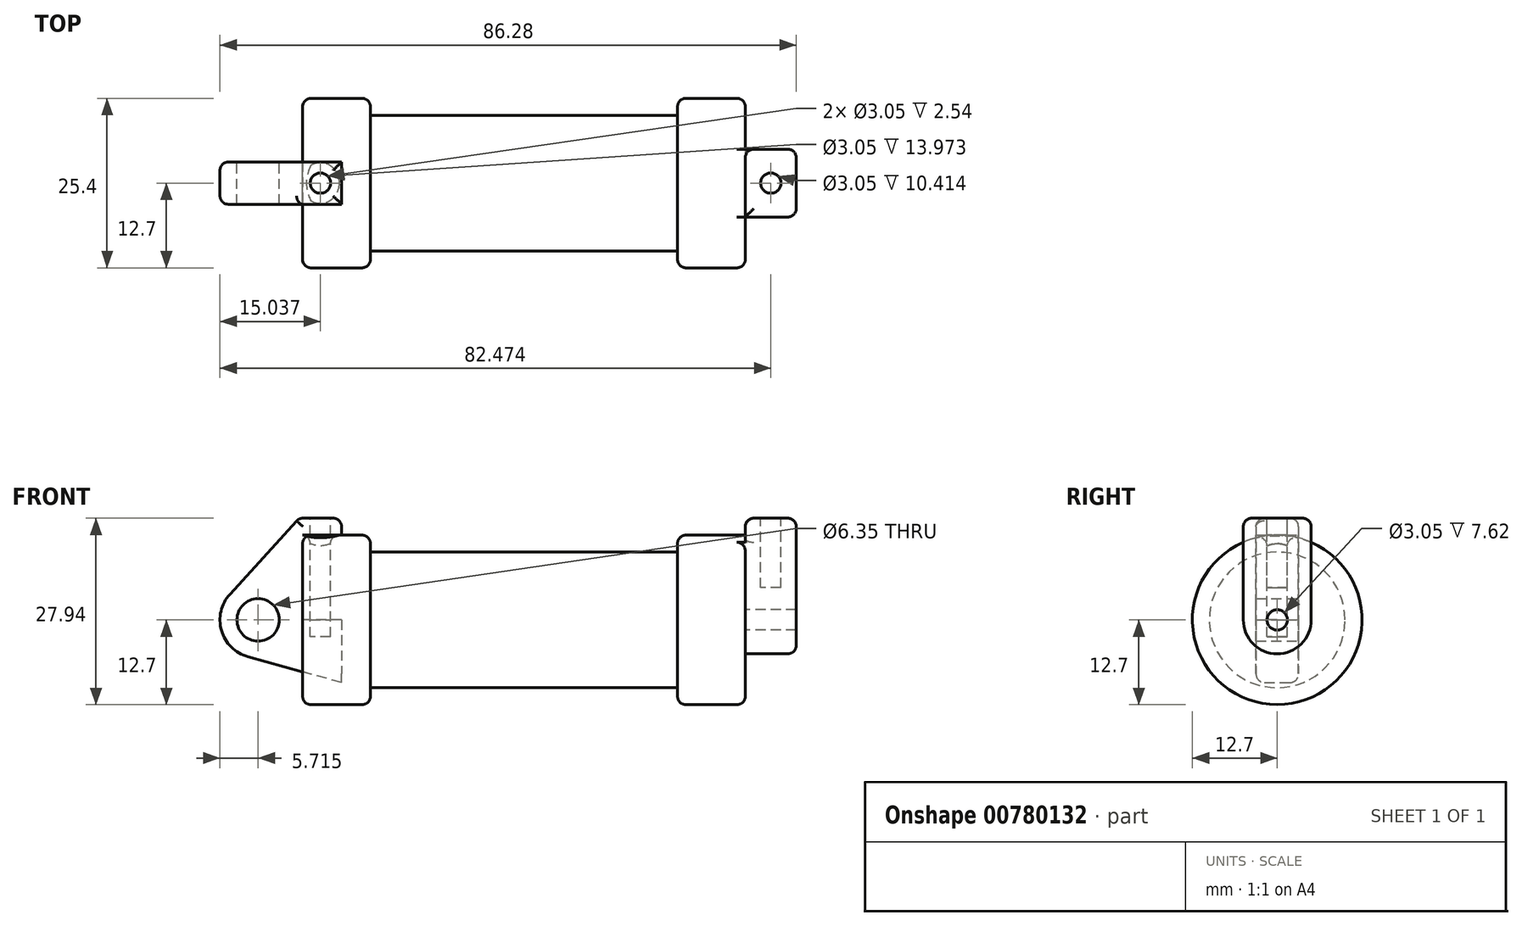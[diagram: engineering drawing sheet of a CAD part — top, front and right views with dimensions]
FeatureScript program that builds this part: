
annotation { "Feature Type Name" : "Feature", "Feature Type Description" : "" }
export const myFeature = defineFeature(function(context is Context, id is Id, definition is map)
    precondition{}
    {
        {
            var Q0;
            Q0=qCreatedBy(makeId("Front.planeOp"),FACE);
            var sketch = newSketch(context, id + "F0", { "sketchPlane" : qUnion([Q0])});
            skLineSegment(sketch, "E0", {"start": v(0, 0) * mm, "end": v(0, 12.7) * mm});
            skLineSegment(sketch, "E1", {"start": v(0, 12.7) * mm, "end": v(10.16, 12.7) * mm});
            skLineSegment(sketch, "E2", {"start": v(10.16, 12.7) * mm, "end": v(10.16, 10.16) * mm});
            skLineSegment(sketch, "E3", {"start": v(10.16, 10.16) * mm, "end": v(56.13, 10.16) * mm});
            skLineSegment(sketch, "E4", {"start": v(56.13, 10.16) * mm, "end": v(56.13, 12.7) * mm});
            skLineSegment(sketch, "E5", {"start": v(56.13, 12.7) * mm, "end": v(66.3, 12.7) * mm});
            skLineSegment(sketch, "E6", {"start": v(66.3, 12.7) * mm, "end": v(66.3, 0) * mm});
            skLineSegment(sketch, "E7", {"start": v(66.3, 0) * mm, "end": v(0, 0) * mm});
            skLineSegment(sketch, "E8", {"start": v(5.84, 15.24) * mm, "end": v(-0.5, 15.24) * mm});
            skLineSegment(sketch, "E9", {"start": v(-0.5, 15.24) * mm, "end": v(-10.88, 3.85) * mm});
            skLineSegment(sketch, "E10", {"start": v(0, 0) * mm, "end": v(-6.65, 0) * mm});
            skCircle(sketch, "E11", {"center": v(-6.65, 0) * mm, "radius": 5.72 * mm});
            skCircle(sketch, "E12", {"center": v(-6.65, 0) * mm, "radius": 3.18 * mm});
            skLineSegment(sketch, "E13", {"start": v(5.84, 15.24) * mm, "end": v(5.84, -9.4) * mm});
            skLineSegment(sketch, "E14", {"start": v(5.84, -9.4) * mm, "end": v(-8.18, -5.5) * mm});
            skSolve(sketch);
        }
        {
            var Q0;
            {var subQ0=sQuery(id+"F0.wireOp",EDGE,"E2");Q0=makeQuery(id+"F0.imprint","IMPRINT",FACE,{"disambiguationData":[TD([[makeQuery(id+"F0.imprint","IMPRINT",EDGE,{"derivedFrom":subQ0}),-1.0]])]});}
            var Q1;
            {var subQ0=sQuery(id+"F0.wireOp",EDGE,"E0");Q1=makeQuery(id+"F0.imprint","IMPRINT",FACE,{"disambiguationData":[TD([[makeQuery(id+"F0.imprint","IMPRINT",EDGE,{"derivedFrom":subQ0}),-1.0]])]});}
            var Q2;
            Q2=sQuery(id+"F0.wireOp",EDGE,"E7");
            revolve(context, id + "F1", {"entities" : qUnion([Q0, Q1]), "axis" : qUnion([Q2]), "revolveType" : RevolveType.FULL});
        }
        {
            var Q0;
            {var subQ1=sQuery(id+"F0.wireOp",EDGE,"E0");Q0=makeQuery(id+"F0.imprint","IMPRINT",FACE,{"disambiguationData":[TD([[makeQuery(id+"F0.imprint","IMPRINT",EDGE,{"derivedFrom":subQ1}),1.0]])]});}
            var Q1;
            {var subQ5=sQuery(id+"F0.wireOp",EDGE,"E12");Q1=makeQuery(id+"F0.imprint","IMPRINT",FACE,{"disambiguationData":[TD([[makeQuery(id+"F0.imprint","IMPRINT",EDGE,{"derivedFrom":subQ5}),-1.0]])]});}
            var Q2;
            {var subQ0=sQuery(id+"F0.wireOp",EDGE,"E14");Q2=makeQuery(id+"F0.imprint","IMPRINT",FACE,{"disambiguationData":[TD([[makeQuery(id+"F0.imprint","IMPRINT",EDGE,{"derivedFrom":subQ0}),-1.0]])]});}
            extrude(context, id + "F2", {"entities" : qUnion([Q0, Q1, Q2]), "depth" : 6.35 * mm, "offsetDistance" : 25.4 * mm, "symmetric" : true});
        }
        {
            var Q0;
            Q0=makeQuery(id+"F1.opRevolve","SWEPT_FACE",FACE,{"disambiguationData":[OSD([sQuery(id+"F0.wireOp",EDGE,"E6")])]});
            var sketch = newSketch(context, id + "F3", { "sketchPlane" : qUnion([Q0])});
            skCircle(sketch, "E15", {"center": v(0, 0) * mm, "radius": 1.52 * mm});
            skCircle(sketch, "E16", {"center": v(0, 0) * mm, "radius": 5.08 * mm});
            skLineSegment(sketch, "E17", {"start": v(5.08, 0) * mm, "end": v(5.08, 15.24) * mm});
            skLineSegment(sketch, "E18", {"start": v(5.08, 15.24) * mm, "end": v(-5.08, 15.24) * mm});
            skLineSegment(sketch, "E19", {"start": v(-5.08, 0) * mm, "end": v(-5.08, 15.24) * mm});
            skSolve(sketch);
        }
        {
            var Q0;
            Q0=qSketchRegion(id+"F3",true);
            extrude(context, id + "F4", {"entities" : qUnion([Q0]), "operationType" : NewBodyOperationType.ADD, "depth" : 7.62 * mm, "offsetDistance" : 25.4 * mm});
        }
        {
            var Q0;
            Q0=makeQuery(id+"F2.opExtrude","SWEPT_FACE",FACE,{"disambiguationData":[OSD([sQuery(id+"F0.wireOp",EDGE,"E8")])]});
            var sketch = newSketch(context, id + "F5", { "sketchPlane" : qUnion([Q0])});
            skCircle(sketch, "E20", {"center": v(2.67, 0) * mm, "radius": 1.52 * mm});
            skPoint(sketch, "E20.centerSnap0", {"position": v(5.84, 0) * mm});
            skPoint(sketch, "E20.centerSnap1", {"position": v(2.67, 3.18) * mm});
            skSolve(sketch);
        }
        {
            var Q0;
            Q0=makeQuery(id+"F4.opExtrude","SWEPT_FACE",FACE,{"disambiguationData":[OSD([sQuery(id+"F3.wireOp",EDGE,"E18")])]});
            var sketch = newSketch(context, id + "F6", { "sketchPlane" : qUnion([Q0])});
            skCircle(sketch, "E21", {"center": v(70.1, 0) * mm, "radius": 1.52 * mm});
            skPoint(sketch, "E21.centerSnap0", {"position": v(73.91, 0) * mm});
            skPoint(sketch, "E21.centerSnap1", {"position": v(70.1, 5.08) * mm});
            skSolve(sketch);
        }
        {
            var Q0;
            Q0=makeQuery(id+"F5.imprint","IMPRINT",FACE,{"disambiguationData":[TD([[makeQuery(id+"F5.imprint","IMPRINT",EDGE,{"derivedFrom":sQuery(id+"F5.wireOp",EDGE,"E20")}),1.0]])]});
            var Q1;
            Q1=sQuery(id+"F5.wireOp",EDGE,"E20");
            extrude(context, id + "F7", {"entities" : qUnion([Q0]), "operationType" : NewBodyOperationType.REMOVE, "surfaceEntities" : qUnion([Q1]), "oppositeDirection" : true, "depth" : 17.78 * mm, "offsetDistance" : 25.4 * mm});
        }
        {
            var Q0;
            Q0=makeQuery(id+"F6.imprint","IMPRINT",FACE,{"disambiguationData":[TD([[makeQuery(id+"F6.imprint","IMPRINT",EDGE,{"derivedFrom":sQuery(id+"F6.wireOp",EDGE,"E21")}),1.0]])]});
            extrude(context, id + "F8", {"entities" : qUnion([Q0]), "operationType" : NewBodyOperationType.REMOVE, "oppositeDirection" : true, "depth" : 10.4 * mm, "offsetDistance" : 25.4 * mm});
        }
        {
            var Q0;
            {var subQ0=sQuery(id+"F0.wireOp",EDGE,"E5");var subQ1=sQuery(id+"F0.wireOp",EDGE,"E6");Q0=makeQuery(id+"F4.boolean.opBoolean","SPLIT",EDGE,{"disambiguationData":[topologyDisambiguationEdgeConnected([makeQuery(id+"F1.opRevolve","SWEPT_FACE",FACE,{"disambiguationData":[OSD([subQ1])]})])],"derivedFrom":makeQuery(id+"F1.opRevolve","SWEPT_EDGE",EDGE,{"disambiguationData":[OSD([subQ0,subQ1])]})});}
            fillet(context, id + "F9", {"entities" : qUnion([Q0]), "radius" : 1.27 * mm, "tangentPropagation" : true, "allowEdgeOverflow" : false});
        }
        {
            var Q0;
            Q0=makeQuery(id+"F2.opExtrude","CAP_EDGE",EDGE,{"disambiguationData":[OSD([sQuery(id+"F0.wireOp",EDGE,"E9")])],"isStart":false});
            fillet(context, id + "F10", {"entities" : qUnion([Q0]), "radius" : 1.27 * mm, "tangentPropagation" : true, "allowEdgeOverflow" : false});
        }
        {
            var Q0;
            Q0=makeQuery(id+"F1.opRevolve","SWEPT_FACE",FACE,{"disambiguationData":[OSD([sQuery(id+"F0.wireOp",EDGE,"E1")])]});
            var Q1;
            Q1=makeQuery(id+"F2.opExtrude","CAP_EDGE",EDGE,{"disambiguationData":[OSD([sQuery(id+"F0.wireOp",EDGE,"E9")])],"isStart":true});
            var Q2;
            Q2=makeQuery(id+"F2.opExtrude","CAP_EDGE",EDGE,{"disambiguationData":[OSD([sQuery(id+"F0.wireOp",EDGE,"E8")])],"isStart":true});
            var Q3;
            Q3=makeQuery(id+"F2.opExtrude","SWEPT_EDGE",EDGE,{"disambiguationData":[OSD([sQuery(id+"F0.wireOp",EDGE,"E8"),sQuery(id+"F0.wireOp",EDGE,"E13")])]});
            var Q4;
            Q4=makeQuery(id+"F2.opExtrude","CAP_EDGE",EDGE,{"disambiguationData":[OSD([sQuery(id+"F0.wireOp",EDGE,"E8")])],"isStart":false});
            var Q5;
            Q5=makeQuery(id+"F1.opRevolve","SWEPT_EDGE",EDGE,{"disambiguationData":[OSD([sQuery(id+"F0.wireOp",EDGE,"E4"),sQuery(id+"F0.wireOp",EDGE,"E5")])]});
            var Q6;
            Q6=makeQuery(id+"F4.opExtrude","CAP_EDGE",EDGE,{"disambiguationData":[OSD([sQuery(id+"F3.wireOp",EDGE,"E17")])],"isStart":false});
            var Q7;
            Q7=makeQuery(id+"F4.opExtrude","CAP_EDGE",EDGE,{"disambiguationData":[OSD([sQuery(id+"F3.wireOp",EDGE,"E18")])],"isStart":true});
            var Q8;
            Q8=makeQuery(id+"F4.opExtrude","CAP_EDGE",EDGE,{"disambiguationData":[OSD([sQuery(id+"F3.wireOp",EDGE,"E18")])],"isStart":false});
            var Q9;
            Q9=makeQuery(id+"F4.opExtrude","SWEPT_EDGE",EDGE,{"disambiguationData":[OSD([sQuery(id+"F3.wireOp",EDGE,"E17"),sQuery(id+"F3.wireOp",EDGE,"E18")])]});
            var Q10;
            Q10=makeQuery(id+"F4.opExtrude","SWEPT_EDGE",EDGE,{"disambiguationData":[OSD([sQuery(id+"F3.wireOp",EDGE,"E18"),sQuery(id+"F3.wireOp",EDGE,"E19")])]});
            fillet(context, id + "F11", {"entities" : qUnion([Q0, Q1, Q2, Q3, Q4, Q5, Q6, Q7, Q8, Q9, Q10]), "radius" : 1.27 * mm, "tangentPropagation" : true, "allowEdgeOverflow" : false});
        }
        {
            var Q0;
            {var subQ0=sQuery(id+"F3.wireOp",EDGE,"E17");Q0=makeQuery(id+"F4.boolean.opBoolean","SPLIT",EDGE,{"disambiguationData":[topologyDisambiguationEdgeConnected([makeQuery(id+"F1.opRevolve","SWEPT_FACE",FACE,{"disambiguationData":[OSD([sQuery(id+"F0.wireOp",EDGE,"E6")])]})])],"derivedFrom":makeQuery(id+"F4.opExtrude","CAP_EDGE",EDGE,{"disambiguationData":[OSD([subQ0])],"isStart":true})});}
            fillet(context, id + "F12", {"entities" : qUnion([Q0]), "radius" : 1.27 * mm, "tangentPropagation" : true, "allowEdgeOverflow" : false});
        }
    });
